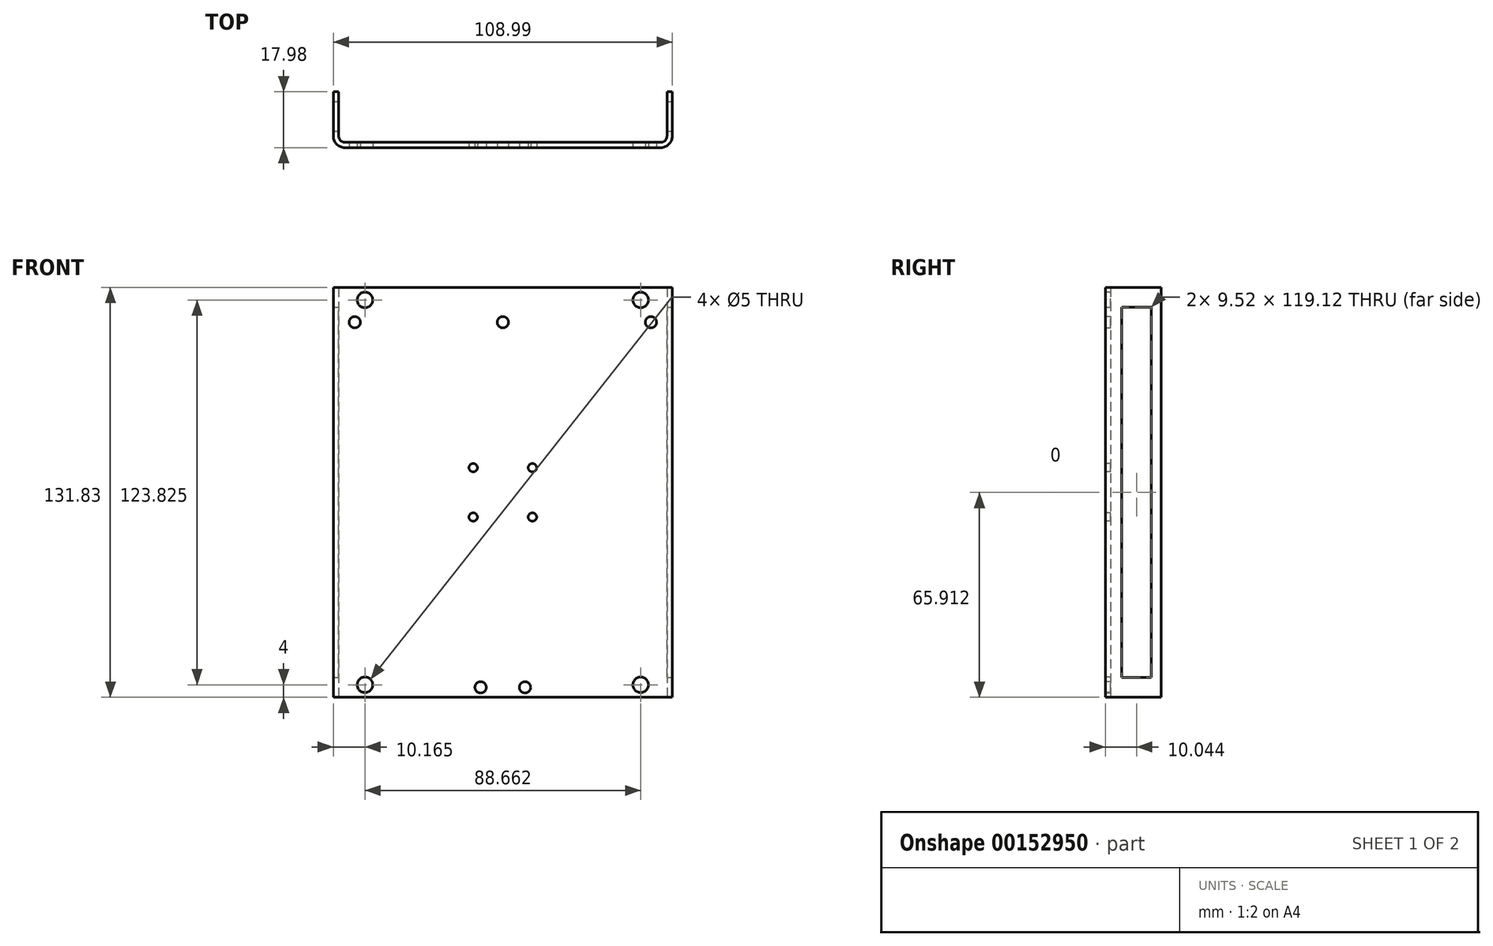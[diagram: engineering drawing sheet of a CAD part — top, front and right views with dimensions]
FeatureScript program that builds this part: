
annotation { "Feature Type Name" : "Feature", "Feature Type Description" : "" }
export const myFeature = defineFeature(function(context is Context, id is Id, definition is map)
    precondition{}
    {
        {
            var Q0;
            Q0=qCreatedBy(makeId("Top.planeOp"),FACE);
            var sketch = newSketch(context, id + "F0", { "sketchPlane" : qUnion([Q0])});
            skLineSegment(sketch, "E0.bottom", {"start": v(0, 0) * mm, "end": v(-105.57, 0) * mm});
            skLineSegment(sketch, "E0.top", {"start": v(1.7, -1.7) * mm, "end": v(-107.28, -1.7) * mm});
            skLineSegment(sketch, "E1.top", {"start": v(-105.57, 16.27) * mm, "end": v(-107.28, 16.27) * mm});
            skLineSegment(sketch, "E1.left", {"start": v(-105.57, 0) * mm, "end": v(-105.57, 16.27) * mm});
            skLineSegment(sketch, "E1.right", {"start": v(-107.28, -1.7) * mm, "end": v(-107.28, 16.27) * mm});
            skLineSegment(sketch, "E2.top", {"start": v(0, 16.27) * mm, "end": v(1.7, 16.27) * mm});
            skLineSegment(sketch, "E2.left", {"start": v(0, 0) * mm, "end": v(0, 16.27) * mm});
            skLineSegment(sketch, "E2.right", {"start": v(1.7, -1.7) * mm, "end": v(1.7, 16.27) * mm});
            skLineSegment(sketch, "E3", {"start": v(-52.78, 0) * mm, "end": v(-52.78, -1.7) * mm, "construction": true});
            skSolve(sketch);
        }
        {
            var Q0;
            Q0=qSketchRegion(id+"F0",true);
            extrude(context, id + "F1", {"entities" : qUnion([Q0]), "depth" : 131.83 * mm});
        }
        {
            var Q0;
            Q0=makeQuery(id+"F1.opExtrude","SWEPT_FACE",FACE,{"disambiguationData":[OSD([sQuery(id+"F0.wireOp",EDGE,"E2.right")])]});
            var sketch = newSketch(context, id + "F2", { "sketchPlane" : qUnion([Q0])});
            skLineSegment(sketch, "E4.bottom", {"start": v(13.1, 125.48) * mm, "end": v(3.57, 125.48) * mm});
            skLineSegment(sketch, "E4.top", {"start": v(13.1, 6.35) * mm, "end": v(3.57, 6.35) * mm});
            skLineSegment(sketch, "E4.left", {"start": v(13.1, 125.48) * mm, "end": v(13.1, 6.35) * mm});
            skLineSegment(sketch, "E4.right", {"start": v(3.57, 125.48) * mm, "end": v(3.57, 6.35) * mm});
            skLineSegment(sketch, "E5", {"start": v(13.1, 65.91) * mm, "end": v(16.27, 65.91) * mm, "construction": true});
            skLineSegment(sketch, "E6", {"start": v(8.33, 6.35) * mm, "end": v(8.33, 0) * mm, "construction": true});
            skSolve(sketch);
        }
        {
            var Q0;
            Q0=qSketchRegion(id+"F2",true);
            var Q1;
            Q1=makeQuery(id+"F1.opExtrude","SWEPT_FACE",FACE,{"disambiguationData":[OSD([sQuery(id+"F0.wireOp",EDGE,"E1.right")])]});
            extrude(context, id + "F3", {"entities" : qUnion([Q0]), "operationType" : NewBodyOperationType.REMOVE, "endBound" : BoundingType.UP_TO_SURFACE, "oppositeDirection" : true, "endBoundEntityFace" : qUnion([Q1]), "depth" : 25.4 * mm});
        }
        {
            var Q0;
            Q0=makeQuery(id+"F1.opExtrude","SWEPT_EDGE",EDGE,{"disambiguationData":[OSD([sQuery(id+"F0.wireOp",EDGE,"E0.top"),sQuery(id+"F0.wireOp",EDGE,"E2.right")])]});
            var Q1;
            Q1=makeQuery(id+"F1.opExtrude","SWEPT_EDGE",EDGE,{"disambiguationData":[OSD([sQuery(id+"F0.wireOp",EDGE,"E0.top"),sQuery(id+"F0.wireOp",EDGE,"E1.right")])]});
            var Q2;
            Q2=makeQuery(id+"FqNnmMD7oaRdpTN_1.opExtrude","CAP_EDGE",EDGE,{"disambiguationData":[OSD([sQuery(id+"FY5sMr6MULj5lJw_1.wireOp",EDGE,"W42EfhJi-fDm4-L9BW-folL-irsYfDskuzBk.top")])],"isStart":false});
            fillet(context, id + "F4", {"entities" : qUnion([Q0, Q1, Q2]), "radius" : 3.7 * mm, "tangentPropagation" : true, "allowEdgeOverflow" : false});
        }
        {
            var Q0;
            Q0=makeQuery(id+"F1.opExtrude","SWEPT_EDGE",EDGE,{"disambiguationData":[OSD([sQuery(id+"F0.wireOp",EDGE,"E0.bottom"),sQuery(id+"F0.wireOp",EDGE,"E2.left")])]});
            var Q1;
            Q1=makeQuery(id+"F1.opExtrude","SWEPT_EDGE",EDGE,{"disambiguationData":[OSD([sQuery(id+"F0.wireOp",EDGE,"E0.bottom"),sQuery(id+"F0.wireOp",EDGE,"E1.left")])]});
            var Q2;
            Q2=makeQuery(id+"FINw0yXB7tfJ6ph_1.opExtrude","CAP_EDGE",EDGE,{"disambiguationData":[OSD([sQuery(id+"FXTh39mUIuS7Wju_1.wireOp",EDGE,"hp9PxWrt-gqSh-sbC0-0nHm-23euh1xvblPI.top")])],"isStart":true});
            fillet(context, id + "F5", {"entities" : qUnion([Q0, Q1, Q2]), "radius" : 1.98 * mm, "tangentPropagation" : true, "allowEdgeOverflow" : false});
        }
        {
            var Q0;
            Q0=makeQuery(id+"FqNnmMD7oaRdpTN_1.boolean.opBoolean","MERGE",FACE,{"derivedFrom":[makeQuery(id+"F1.opExtrude","SWEPT_FACE",FACE,{"disambiguationData":[OSD([sQuery(id+"F0.wireOp",EDGE,"E0.top")])]}),makeQuery(id+"FqNnmMD7oaRdpTN_1.opExtrude","SWEPT_FACE",FACE,{"disambiguationData":[OSD([sQuery(id+"FY5sMr6MULj5lJw_1.wireOp",EDGE,"W42EfhJi-fDm4-L9BW-folL-irsYfDskuzBk.top")])]})]});
            var sketch = newSketch(context, id + "F6", { "sketchPlane" : qUnion([Q0])});
            skLineSegment(sketch, "E7", {"start": v(-52.78, 131.83) * mm, "end": v(-52.78, 120.65) * mm, "construction": true});
            skLineSegment(sketch, "E8", {"start": v(-111.58, 120.65) * mm, "end": v(-100.4, 120.65) * mm, "construction": true});
            skLineSegment(sketch, "E9", {"start": v(-100.4, 120.65) * mm, "end": v(-5.16, 120.65) * mm, "construction": true});
            skLineSegment(sketch, "E10", {"start": v(-5.16, 120.65) * mm, "end": v(-1.98, 120.65) * mm, "construction": true});
            skCircle(sketch, "E11", {"center": v(-52.78, 120.65) * mm, "radius": 1.83 * mm});
            skCircle(sketch, "E12", {"center": v(-5.16, 120.65) * mm, "radius": 1.83 * mm});
            skCircle(sketch, "E13", {"center": v(-100.4, 120.65) * mm, "radius": 1.83 * mm});
            skLineSegment(sketch, "E14", {"start": v(-52.78, 0) * mm, "end": v(-52.78, 3.17) * mm, "construction": true});
            skLineSegment(sketch, "E15", {"start": v(-45.64, 3.17) * mm, "end": v(-59.93, 3.17) * mm, "construction": true});
            skCircle(sketch, "E16", {"center": v(-45.64, 3.17) * mm, "radius": 1.83 * mm});
            skCircle(sketch, "E17", {"center": v(-59.93, 3.17) * mm, "radius": 1.83 * mm});
            skSolve(sketch);
        }
        {
            var Q0;
            Q0=qSketchRegion(id+"F6",true);
            var Q1;
            Q1=makeQuery(id+"FqNnmMD7oaRdpTN_1.boolean.opBoolean","MERGE",FACE,{"derivedFrom":[makeQuery(id+"F1.opExtrude","SWEPT_FACE",FACE,{"disambiguationData":[OSD([sQuery(id+"F0.wireOp",EDGE,"E0.bottom")])]}),makeQuery(id+"FqNnmMD7oaRdpTN_1.opExtrude","SWEPT_FACE",FACE,{"disambiguationData":[OSD([sQuery(id+"FY5sMr6MULj5lJw_1.wireOp",EDGE,"W42EfhJi-fDm4-L9BW-folL-irsYfDskuzBk.bottom")])]})]});
            extrude(context, id + "F7", {"entities" : qUnion([Q0]), "operationType" : NewBodyOperationType.REMOVE, "endBound" : BoundingType.UP_TO_SURFACE, "oppositeDirection" : true, "endBoundEntityFace" : qUnion([Q1]), "depth" : 25.4 * mm});
        }
        {
            var Q0;
            Q0=makeQuery(id+"F1.opExtrude","SWEPT_FACE",FACE,{"disambiguationData":[OSD([sQuery(id+"F0.wireOp",EDGE,"E0.top")])]});
            var sketch = newSketch(context, id + "F8", { "sketchPlane" : qUnion([Q0])});
            skLineSegment(sketch, "E18", {"start": v(-1.98, 65.91) * mm, "end": v(-103.58, 65.91) * mm, "construction": true});
            skLineSegment(sketch, "E19.bottom", {"start": v(-1.98, 131.83) * mm, "end": v(-8.45, 131.83) * mm, "construction": true});
            skLineSegment(sketch, "E19.top", {"start": v(-1.98, 127.83) * mm, "end": v(-8.45, 127.83) * mm, "construction": true});
            skLineSegment(sketch, "E19.left", {"start": v(-1.98, 131.83) * mm, "end": v(-1.98, 127.83) * mm, "construction": true});
            skLineSegment(sketch, "E19.right", {"start": v(-8.45, 131.83) * mm, "end": v(-8.45, 127.83) * mm, "construction": true});
            skLineSegment(sketch, "E20.bottom", {"start": v(-8.45, 127.83) * mm, "end": v(-97.11, 127.83) * mm, "construction": true});
            skLineSegment(sketch, "E20.top", {"start": v(-8.45, 4) * mm, "end": v(-97.11, 4) * mm, "construction": true});
            skLineSegment(sketch, "E20.left", {"start": v(-8.45, 127.83) * mm, "end": v(-8.45, 4) * mm, "construction": true});
            skLineSegment(sketch, "E20.right", {"start": v(-97.11, 127.83) * mm, "end": v(-97.11, 4) * mm, "construction": true});
            skPoint(sketch, "E20.middle", {"position": v(-52.78, 65.91) * mm});
            skCircle(sketch, "E21", {"center": v(-8.45, 127.83) * mm, "radius": 2.5 * mm});
            skCircle(sketch, "E22", {"center": v(-8.45, 4) * mm, "radius": 2.5 * mm});
            skCircle(sketch, "E23", {"center": v(-97.11, 4) * mm, "radius": 2.5 * mm});
            skCircle(sketch, "E24", {"center": v(-97.11, 127.83) * mm, "radius": 2.5 * mm});
            skSolve(sketch);
        }
        {
            var Q0;
            Q0 = qSketchRegion(id + "F8", true);
            var Q1;
            Q1=makeQuery(id+"F1.opExtrude","SWEPT_FACE",FACE,{"disambiguationData":[OSD([sQuery(id+"F0.wireOp",EDGE,"E0.bottom")])]});
            extrude(context, id + "F9", {"entities" : qUnion([Q0]), "operationType" : NewBodyOperationType.REMOVE, "endBound" : BoundingType.UP_TO_SURFACE, "oppositeDirection" : true, "endBoundEntityFace" : qUnion([Q1]), "depth" : 25.4 * mm});
        }
        {
            var Q0;
            Q0=makeQuery(id+"F1.opExtrude","SWEPT_FACE",FACE,{"disambiguationData":[OSD([sQuery(id+"F0.wireOp",EDGE,"E0.top")])]});
            var sketch = newSketch(context, id + "F10", { "sketchPlane" : qUnion([Q0])});
            skLineSegment(sketch, "E25", {"start": v(-52.78, 0) * mm, "end": v(-52.78, 131.83) * mm, "construction": true});
            skLineSegment(sketch, "E26", {"start": v(-45.64, 3.17) * mm, "end": v(-52.78, 3.17) * mm, "construction": true});
            skLineSegment(sketch, "E27", {"start": v(-52.78, 3.17) * mm, "end": v(-59.93, 3.17) * mm, "construction": true});
            skCircle(sketch, "E28", {"center": v(-43.26, 57.98) * mm, "radius": 1.35 * mm});
            skCircle(sketch, "E29", {"center": v(-43.26, 73.85) * mm, "radius": 1.35 * mm});
            skLineSegment(sketch, "E30.bottom", {"start": v(-43.26, 57.98) * mm, "end": v(-43.26, 73.85) * mm, "construction": true});
            skLineSegment(sketch, "E30.top", {"start": v(-62.3, 57.98) * mm, "end": v(-62.3, 73.85) * mm, "construction": true});
            skLineSegment(sketch, "E30.left", {"start": v(-43.26, 57.98) * mm, "end": v(-62.3, 57.98) * mm, "construction": true});
            skLineSegment(sketch, "E30.right", {"start": v(-43.26, 73.85) * mm, "end": v(-62.3, 73.85) * mm, "construction": true});
            skPoint(sketch, "E30.middle", {"position": v(-52.78, 65.91) * mm});
            skCircle(sketch, "E31", {"center": v(-62.3, 57.98) * mm, "radius": 1.35 * mm});
            skCircle(sketch, "E32", {"center": v(-62.3, 73.85) * mm, "radius": 1.35 * mm});
            skSolve(sketch);
        }
        {
            var Q0;
            Q0 = qSketchRegion(id + "F10", true);
            var Q1;
            Q1=makeQuery(id+"F1.opExtrude","SWEPT_FACE",FACE,{"disambiguationData":[OSD([sQuery(id+"F0.wireOp",EDGE,"E0.bottom")])]});
            extrude(context, id + "F11", {"entities" : qUnion([Q0]), "operationType" : NewBodyOperationType.REMOVE, "endBound" : BoundingType.UP_TO_SURFACE, "oppositeDirection" : true, "endBoundEntityFace" : qUnion([Q1]), "depth" : 25.4 * mm});
        }
    });
